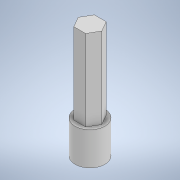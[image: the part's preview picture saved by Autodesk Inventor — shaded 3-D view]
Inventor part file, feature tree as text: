
AUTODESK INVENTOR PART (.ipt)
format: ipt  version: 2021 (Build 250183000, 183)  size: 149,504 bytes
history: native  units: mm
features: sketch x11, extrude x7, hole x1
ambient origin geometry x8: Origin, YZ Plane, XZ Plane, XY Plane, X Axis, Y Axis, Z Axis, Center Point
bodies: Solid1 (feature_tree), Solid2 (feature_tree)
feature tree (19):
  extrude  "Extrusion2"  Depth=2.38mm TaperAngle=0.0deg
  extrude  "Extrusion3"  Depth=7.0mm
  extrude  "Extrusion4"  Depth=9.0mm
  extrude  "Extrusion5"  Depth=10.0mm
  extrude  "Extrusion10"  Depth=10.0mm TaperAngle=0.0deg
  sketch  "Sketch8"  dims[d21=2.0mm d22=2.25mm d23=0.0mm]
  extrude  "Extrusion6"  Depth=7.16mm
  hole  "Hole1"  [1 undecoded]
  extrude  "Extrusion1"  Depth=2.25mm TaperAngle=0.0deg
  sketch  "Sketch2"  dims[d3=4.0mm d4=7.0mm]
  sketch  "Sketch3"  dims[d5=3.5mm d6=9.0mm]
  sketch  "Sketch1"  dims[d0=25.0mm d1=2.38mm d2=0.0mm]
  sketch  "Sketch4"  dims[d7=10.0mm d8=0.0mm d9=4.0mm]
  sketch  "Sketch5"  dims[d10=3.5mm d11=10.0mm d12=0.0mm]
  sketch  "Sketch6"  dims[d13=2.0mm d14=0.0mm d15=7.16mm]
  sketch  "Sketch7"  dims[d16=24.5mm d17=0.0mm d18=0.75mm d19=0.0mm]
  sketch  "Sketch9"  dims[d24=2.0mm d25=6.0mm d26=4.0mm d27=2.0mm d28=90.0deg d29=3.33mm d30=0.0mm]
  sketch  "Sketch10"  dims[d38=2.0mm]
  sketch  "Sketch14"  dims[d39=4.0mm d40=0.0mm d34=0.5mm d35=0.872665mm d36=0.5mm d37=0.872665mm d41=0.872665mm]
note: 1 required parameter value undecoded (feature->parameter linkage not recoverable at this tier; creation-order binding heuristic only, values carry confidence <= 0.55)
